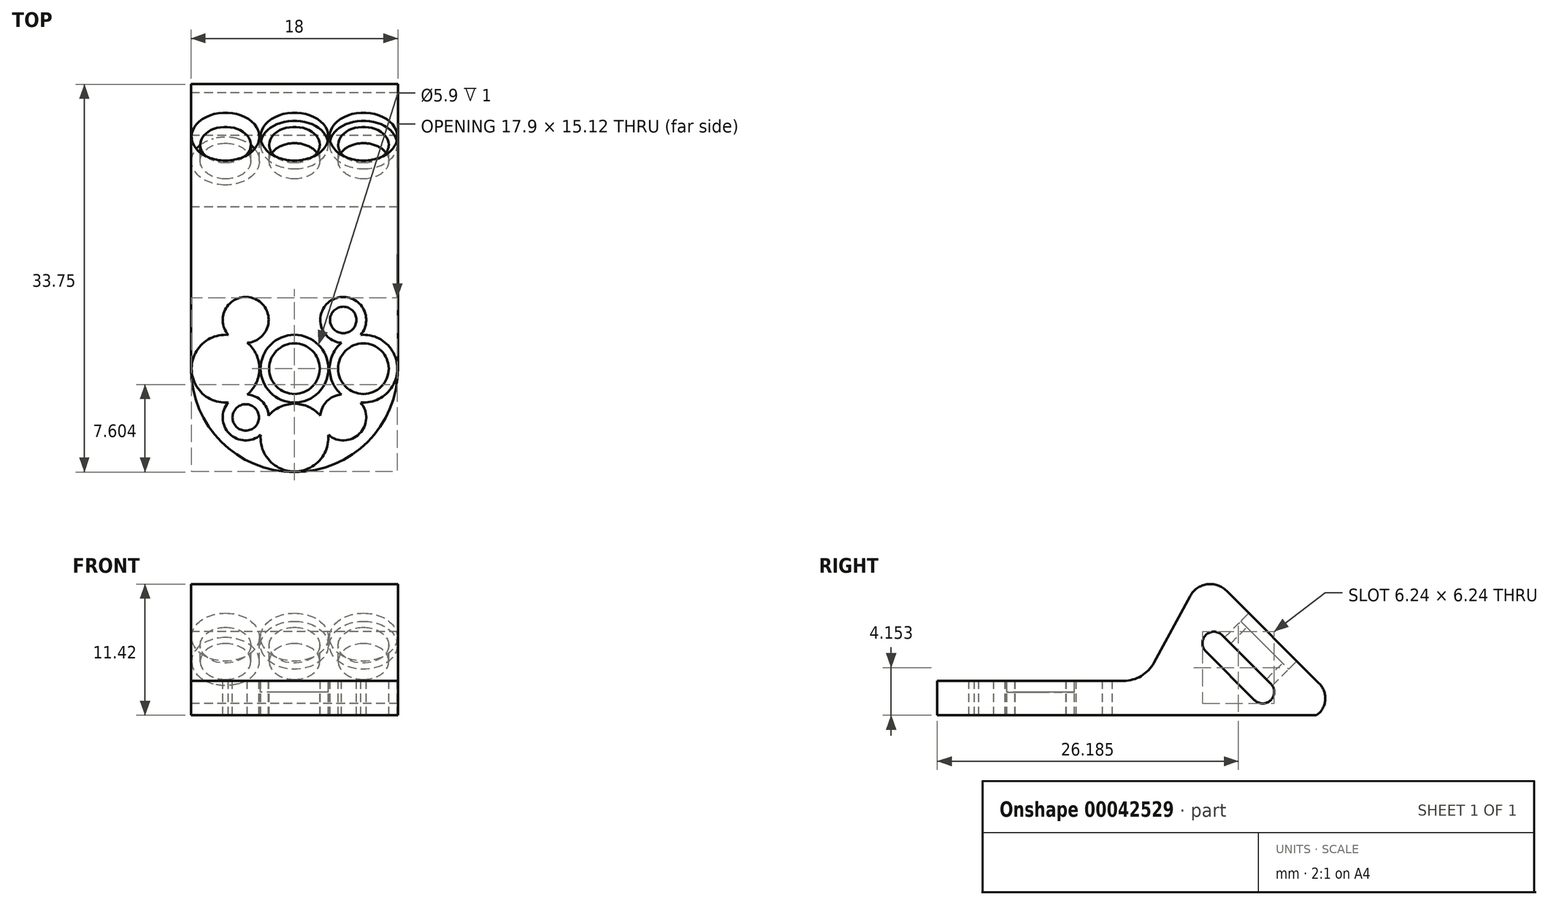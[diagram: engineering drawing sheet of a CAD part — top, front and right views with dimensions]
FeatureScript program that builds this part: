
annotation { "Feature Type Name" : "Feature", "Feature Type Description" : "" }
export const myFeature = defineFeature(function(context is Context, id is Id, definition is map)
    precondition{}
    {
        {
            var Q0;
            Q0=qCreatedBy(makeId("Right.planeOp"),FACE);
            var sketch = newSketch(context, id + "F0", { "sketchPlane" : qUnion([Q0])});
            skPoint(sketch, "E0", {"position": v(-20.22, 0) * mm});
            skLineSegment(sketch, "E1", {"start": v(-20.22, 0) * mm, "end": v(12.78, 0) * mm});
            skPoint(sketch, "E2", {"position": v(0, 0) * mm});
            skLineSegment(sketch, "E3", {"start": v(13, 2.78) * mm, "end": v(4.94, 10.83) * mm});
            skLineSegment(sketch, "E4", {"start": v(-20.22, 0) * mm, "end": v(-20.22, 3) * mm});
            skLineSegment(sketch, "E5", {"start": v(-20.22, 3) * mm, "end": v(-4.01, 3) * mm});
            skPoint(sketch, "E6", {"position": v(9.41, 6.36) * mm});
            skLineSegment(sketch, "E7", {"start": v(8.8, 2.74) * mm, "end": v(4.55, 6.98) * mm});
            skLineSegment(sketch, "E8", {"start": v(3.14, 6.98) * mm, "end": v(3.14, 6.98) * mm});
            skLineSegment(sketch, "E9", {"start": v(8.8, 1.32) * mm, "end": v(8.8, 1.32) * mm});
            skLineSegment(sketch, "E10", {"start": v(7.38, 1.32) * mm, "end": v(3.14, 5.57) * mm});
            skLineSegment(sketch, "E11", {"start": v(-1.37, 4.57) * mm, "end": v(1.77, 10.37) * mm});
            skPoint(sketch, "E12.visualSharp", {"position": v(-2.22, 3) * mm});
            skArc(sketch, "E12.filletArc", {"start": v(-4.01, 3) * mm, "mid": v(-2.48, 3.42) * mm, "end": v(-1.37, 4.57) * mm});
            skPoint(sketch, "E13.visualSharp", {"position": v(3.05, 12.73) * mm});
            skArc(sketch, "E13.filletArc", {"start": v(4.94, 10.83) * mm, "mid": v(3.24, 11.4) * mm, "end": v(1.77, 10.37) * mm});
            skPoint(sketch, "E14", {"position": v(12.78, 0) * mm});
            skPoint(sketch, "E15", {"position": v(13, 2.78) * mm});
            skPoint(sketch, "E16.orphan", {"position": v(15.78, 0) * mm});
            skArc(sketch, "E17", {"start": v(12.78, 0) * mm, "mid": v(13.53, 1.34) * mm, "end": v(13, 2.78) * mm});
            skPoint(sketch, "E18.visualSharp", {"position": v(8.09, 0.62) * mm});
            skArc(sketch, "E18.filletArc", {"start": v(7.38, 1.32) * mm, "mid": v(8.09, 1.03) * mm, "end": v(8.8, 1.32) * mm});
            skPoint(sketch, "E19.visualSharp", {"position": v(9.5, 2.03) * mm});
            skArc(sketch, "E19.filletArc", {"start": v(8.8, 1.32) * mm, "mid": v(9.09, 2.03) * mm, "end": v(8.8, 2.74) * mm});
            skPoint(sketch, "E20.visualSharp", {"position": v(2.43, 6.27) * mm});
            skArc(sketch, "E20.filletArc", {"start": v(3.14, 6.98) * mm, "mid": v(2.84, 6.27) * mm, "end": v(3.14, 5.57) * mm});
            skPoint(sketch, "E21.visualSharp", {"position": v(3.84, 7.69) * mm});
            skArc(sketch, "E21.filletArc", {"start": v(4.55, 6.98) * mm, "mid": v(3.84, 7.27) * mm, "end": v(3.14, 6.98) * mm});
            skLineSegment(sketch, "E22", {"start": v(7.38, 1.32) * mm, "end": v(8.8, 2.74) * mm});
            skSolve(sketch);
        }
        {
            var Q0;
            Q0=makeQuery(id+"F0.imprint","IMPRINT",FACE,{"disambiguationData":[TD([[makeQuery(id+"F0.imprint","IMPRINT",EDGE,{"derivedFrom":sQuery(id+"F0.wireOp",EDGE,"E1")}),1.0]])]});
            extrude(context, id + "F1", {"entities" : qUnion([Q0]), "depth" : 18 * mm});
        }
        {
            var Q0;
            Q0=makeQuery(id+"F1.opExtrude","SWEPT_FACE",FACE,{"disambiguationData":[OSD([sQuery(id+"F0.wireOp",EDGE,"E5")])]});
            var sketch = newSketch(context, id + "F2", { "sketchPlane" : qUnion([Q0])});
            skPoint(sketch, "E23", {"position": v(9, -11.22) * mm});
            skCircle(sketch, "E24", {"center": v(9, -11.22) * mm, "radius": 2.95 * mm});
            skCircle(sketch, "E25", {"center": v(9, -11.22) * mm, "radius": 2.2 * mm});
            skLineSegment(sketch, "E26", {"start": v(9, -20.22) * mm, "end": v(9, -4.01) * mm, "construction": true});
            skArc(sketch, "E27", {"start": v(3.24, -8.28) * mm, "mid": v(0.05, -11.22) * mm, "end": v(3.24, -14.17) * mm});
            skPoint(sketch, "E28", {"position": v(0, -11.22) * mm});
            skPoint(sketch, "E28.positionSnap0", {"position": v(0, -12.12) * mm});
            skCircle(sketch, "E29", {"center": v(3, -11.22) * mm, "radius": 2.2 * mm});
            skArc(sketch, "E30.MirrorC", {"start": v(13.1, -13.47) * mm, "mid": v(12.05, -11.22) * mm, "end": v(13.1, -8.98) * mm});
            skCircle(sketch, "E31.MirrorC", {"center": v(15, -11.22) * mm, "radius": 2.2 * mm});
            skArc(sketch, "E32", {"start": v(6.06, -16.99) * mm, "mid": v(9, -20.17) * mm, "end": v(11.94, -16.99) * mm});
            skCircle(sketch, "E33", {"center": v(9, -17.22) * mm, "radius": 2.2 * mm});
            skPoint(sketch, "E34", {"position": v(4.76, -6.98) * mm});
            skArc(sketch, "E35", {"start": v(4.9, -8.98) * mm, "mid": v(5.52, -5.13) * mm, "end": v(3.24, -8.28) * mm});
            skCircle(sketch, "E36", {"center": v(4.76, -6.98) * mm, "radius": 1.15 * mm});
            skCircle(sketch, "E37.MirrorC", {"center": v(13.24, -6.98) * mm, "radius": 1.15 * mm});
            skArc(sketch, "E38.MirrorC", {"start": v(13.1, -8.98) * mm, "mid": v(12.48, -5.13) * mm, "end": v(14.76, -8.28) * mm});
            skLineSegment(sketch, "E39", {"start": v(3, -11.22) * mm, "end": v(15, -11.22) * mm, "construction": true});
            skArc(sketch, "E40.MirrorC", {"start": v(4.9, -13.47) * mm, "mid": v(6.17, -14.05) * mm, "end": v(6.75, -15.32) * mm});
            skCircle(sketch, "E41.MirrorC", {"center": v(4.76, -15.47) * mm, "radius": 1.15 * mm});
            skArc(sketch, "E42.MirrorC", {"start": v(11.94, -16.99) * mm, "mid": v(14.66, -16.88) * mm, "end": v(14.76, -14.17) * mm});
            skCircle(sketch, "E43.MirrorC", {"center": v(13.24, -15.47) * mm, "radius": 1.15 * mm});
            skArc(sketch, "E44.trimOffspring", {"start": v(4.9, -13.47) * mm, "mid": v(5.95, -11.22) * mm, "end": v(4.9, -8.98) * mm});
            skArc(sketch, "E45.trimOffspring", {"start": v(6.06, -16.99) * mm, "mid": v(3.34, -16.88) * mm, "end": v(3.24, -14.17) * mm});
            skArc(sketch, "E46.trimOffspring", {"start": v(11.25, -15.32) * mm, "mid": v(9, -14.27) * mm, "end": v(6.75, -15.32) * mm});
            skArc(sketch, "E47.trimOffspring", {"start": v(13.1, -13.47) * mm, "mid": v(11.83, -14.05) * mm, "end": v(11.25, -15.32) * mm});
            skArc(sketch, "E48.trimOffspring", {"start": v(14.76, -8.28) * mm, "mid": v(17.95, -11.22) * mm, "end": v(14.76, -14.17) * mm});
            skArc(sketch, "E49", {"start": v(0, -11.22) * mm, "mid": v(9, -20.22) * mm, "end": v(18, -11.22) * mm});
            skSolve(sketch);
        }
        {
            var Q0;
            Q0=makeQuery(id+"F2.imprint","IMPRINT",FACE,{"disambiguationData":[TD([[makeQuery(id+"F2.imprint","IMPRINT",EDGE,{"derivedFrom":sQuery(id+"F2.wireOp",EDGE,"E25")}),1.0]])]});
            var Q1;
            Q1=makeQuery(id+"F2.imprint","IMPRINT",FACE,{"disambiguationData":[TD([[makeQuery(id+"F2.imprint","IMPRINT",EDGE,{"derivedFrom":sQuery(id+"F2.wireOp",EDGE,"E29")}),1.0]])]});
            var Q2;
            Q2=makeQuery(id+"F2.imprint","IMPRINT",FACE,{"disambiguationData":[TD([[makeQuery(id+"F2.imprint","IMPRINT",EDGE,{"derivedFrom":sQuery(id+"F2.wireOp",EDGE,"E36")}),1.0]])]});
            var Q3;
            Q3=makeQuery(id+"F2.imprint","IMPRINT",FACE,{"disambiguationData":[TD([[makeQuery(id+"F2.imprint","IMPRINT",EDGE,{"derivedFrom":sQuery(id+"F2.wireOp",EDGE,"E41.MirrorC")}),-1.0]])]});
            var Q4;
            Q4=makeQuery(id+"F2.imprint","IMPRINT",FACE,{"disambiguationData":[TD([[makeQuery(id+"F2.imprint","IMPRINT",EDGE,{"derivedFrom":sQuery(id+"F2.wireOp",EDGE,"E33")}),1.0]])]});
            var Q5;
            Q5=makeQuery(id+"F2.imprint","IMPRINT",FACE,{"disambiguationData":[TD([[makeQuery(id+"F2.imprint","IMPRINT",EDGE,{"derivedFrom":sQuery(id+"F2.wireOp",EDGE,"E43.MirrorC")}),1.0]])]});
            var Q6;
            Q6=makeQuery(id+"F2.imprint","IMPRINT",FACE,{"disambiguationData":[TD([[makeQuery(id+"F2.imprint","IMPRINT",EDGE,{"derivedFrom":sQuery(id+"F2.wireOp",EDGE,"E31.MirrorC")}),-1.0]])]});
            var Q7;
            Q7=makeQuery(id+"F2.imprint","IMPRINT",FACE,{"disambiguationData":[TD([[makeQuery(id+"F2.imprint","IMPRINT",EDGE,{"derivedFrom":sQuery(id+"F2.wireOp",EDGE,"E37.MirrorC")}),-1.0]])]});
            var Q8;
            {var subQ0=sQuery(id+"F0.wireOp",EDGE,"E5");var subQ1=makeQuery(id+"F1.opExtrude","CAP_EDGE",EDGE,{"disambiguationData":[OSD([subQ0])],"isStart":true});var subQ2=sQuery(id+"F2.wireOp",EDGE,"E49");var subQ3=makeQuery(id+"F2.imprint","INTERSECT",VERTEX,{"derivedFrom":[subQ1,subQ2]});Q8=makeQuery(id+"F2.imprint","IMPRINT",FACE,{"disambiguationData":[TD([[makeQuery(id+"F2.imprint","IMPRINT",EDGE,{"disambiguationData":[TD([[subQ3,-1.0]])],"derivedFrom":subQ2}),-1.0]])]});}
            var Q9;
            {var subQ0=sQuery(id+"F0.wireOp",EDGE,"E5");var subQ2=sQuery(id+"F2.wireOp",EDGE,"E49");var subQ4=makeQuery(id+"F1.opExtrude","CAP_EDGE",EDGE,{"disambiguationData":[OSD([subQ0])],"isStart":false});var subQ6=makeQuery(id+"F2.imprint","INTERSECT",VERTEX,{"derivedFrom":[subQ4,subQ2]});Q9=makeQuery(id+"F2.imprint","IMPRINT",FACE,{"disambiguationData":[TD([[makeQuery(id+"F2.imprint","IMPRINT",EDGE,{"disambiguationData":[TD([[subQ6,1.0]])],"derivedFrom":subQ2}),-1.0]])]});}
            extrude(context, id + "F3", {"entities" : qUnion([Q0, Q1, Q2, Q3, Q4, Q5, Q6, Q7, Q8, Q9]), "operationType" : NewBodyOperationType.REMOVE, "endBound" : BoundingType.THROUGH_ALL, "oppositeDirection" : true, "depth" : 25 * mm});
        }
        {
            var Q0;
            Q0=makeQuery(id+"F2.imprint","IMPRINT",FACE,{"disambiguationData":[TD([[makeQuery(id+"F2.imprint","IMPRINT",EDGE,{"derivedFrom":sQuery(id+"F2.wireOp",EDGE,"E27")}),1.0]])]});
            var Q1;
            Q1=makeQuery(id+"F2.imprint","IMPRINT",FACE,{"disambiguationData":[TD([[makeQuery(id+"F2.imprint","IMPRINT",EDGE,{"derivedFrom":sQuery(id+"F2.wireOp",EDGE,"E24")}),1.0]])]});
            extrude(context, id + "F4", {"entities" : qUnion([Q0, Q1]), "operationType" : NewBodyOperationType.REMOVE, "oppositeDirection" : true, "depth" : 1 * mm});
        }
        {
            var Q0;
            Q0=makeQuery(id+"F1.opExtrude","SWEPT_FACE",FACE,{"disambiguationData":[OSD([sQuery(id+"F0.wireOp",EDGE,"E3")])]});
            var sketch = newSketch(context, id + "F5", { "sketchPlane" : qUnion([Q0])});
            skPoint(sketch, "E50", {"position": v(-18, 4.16) * mm});
            skPoint(sketch, "E51", {"position": v(0, -7.23) * mm});
            skPoint(sketch, "E52", {"position": v(0, 4.16) * mm});
            skPoint(sketch, "E53", {"position": v(-18, -7.23) * mm});
            skLineSegment(sketch, "E54", {"start": v(-18, -1.53) * mm, "end": v(0, -1.53) * mm, "construction": true});
            skLineSegment(sketch, "E55", {"start": v(-9, -7.23) * mm, "end": v(-9, 4.16) * mm, "construction": true});
            skPoint(sketch, "E56", {"position": v(-9, -1.53) * mm});
            skCircle(sketch, "E57", {"center": v(-9, -1.53) * mm, "radius": 2.95 * mm});
            skCircle(sketch, "E58", {"center": v(-9, -1.53) * mm, "radius": 2.2 * mm});
            skCircle(sketch, "E59", {"center": v(-15, -1.53) * mm, "radius": 2.95 * mm});
            skCircle(sketch, "E60", {"center": v(-15, -1.53) * mm, "radius": 2.2 * mm});
            skCircle(sketch, "E61.MirrorC", {"center": v(-3, -1.53) * mm, "radius": 2.2 * mm});
            skCircle(sketch, "E62.MirrorC", {"center": v(-3, -1.53) * mm, "radius": 2.95 * mm});
            skSolve(sketch);
        }
        {
            var Q0;
            Q0=makeQuery(id+"F5.imprint","IMPRINT",FACE,{"disambiguationData":[TD([[makeQuery(id+"F5.imprint","IMPRINT",EDGE,{"derivedFrom":sQuery(id+"F5.wireOp",EDGE,"E60")}),1.0]])]});
            var Q1;
            Q1=makeQuery(id+"F5.imprint","IMPRINT",FACE,{"disambiguationData":[TD([[makeQuery(id+"F5.imprint","IMPRINT",EDGE,{"derivedFrom":sQuery(id+"F5.wireOp",EDGE,"E58")}),1.0]])]});
            var Q2;
            Q2=makeQuery(id+"F5.imprint","IMPRINT",FACE,{"disambiguationData":[TD([[makeQuery(id+"F5.imprint","IMPRINT",EDGE,{"derivedFrom":sQuery(id+"F5.wireOp",EDGE,"E61.MirrorC")}),-1.0]])]});
            extrude(context, id + "F6", {"entities" : qUnion([Q0, Q1, Q2]), "operationType" : NewBodyOperationType.REMOVE, "endBound" : BoundingType.UP_TO_NEXT, "oppositeDirection" : true, "depth" : 25 * mm});
        }
        {
            var Q0;
            Q0=makeQuery(id+"F5.imprint","IMPRINT",FACE,{"disambiguationData":[TD([[makeQuery(id+"F5.imprint","IMPRINT",EDGE,{"derivedFrom":sQuery(id+"F5.wireOp",EDGE,"E59")}),1.0]])]});
            var Q1;
            Q1=makeQuery(id+"F5.imprint","IMPRINT",FACE,{"disambiguationData":[TD([[makeQuery(id+"F5.imprint","IMPRINT",EDGE,{"derivedFrom":sQuery(id+"F5.wireOp",EDGE,"E57")}),1.0]])]});
            var Q2;
            Q2=makeQuery(id+"F5.imprint","IMPRINT",FACE,{"disambiguationData":[TD([[makeQuery(id+"F5.imprint","IMPRINT",EDGE,{"derivedFrom":sQuery(id+"F5.wireOp",EDGE,"E61.MirrorC")}),1.0]])]});
            extrude(context, id + "F7", {"entities" : qUnion([Q0, Q1, Q2]), "operationType" : NewBodyOperationType.REMOVE, "oppositeDirection" : true, "depth" : 1 * mm});
        }
    });
